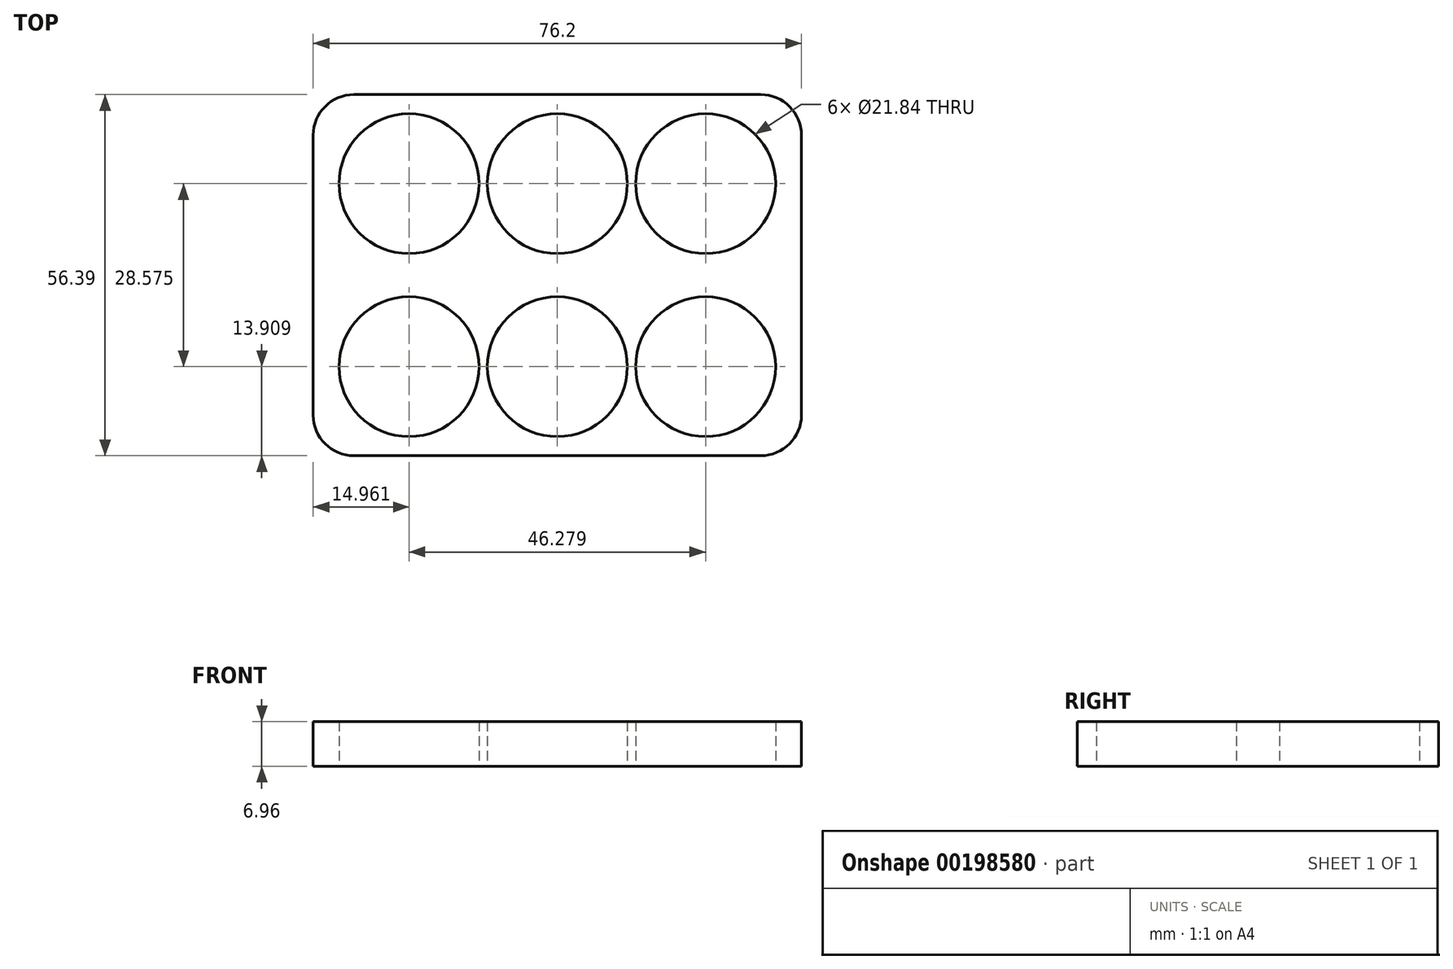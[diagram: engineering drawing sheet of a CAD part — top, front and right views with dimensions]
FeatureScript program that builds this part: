
annotation { "Feature Type Name" : "Feature", "Feature Type Description" : "" }
export const myFeature = defineFeature(function(context is Context, id is Id, definition is map)
    precondition{}
    {
        {
            var Q0;
            Q0=qCreatedBy(makeId("Top.planeOp"),FACE);
            var sketch = newSketch(context, id + "F0", { "sketchPlane" : qUnion([Q0])});
            skLineSegment(sketch, "E0", {"start": v(-31.75, 0) * mm, "end": v(31.75, 0) * mm});
            skArc(sketch, "E1", {"start": v(-31.75, 0) * mm, "mid": v(-36.24, -1.86) * mm, "end": v(-38.1, -6.35) * mm});
            skLineSegment(sketch, "E2", {"start": v(-38.1, -6.35) * mm, "end": v(-38.1, -50.04) * mm});
            skArc(sketch, "E3", {"start": v(-38.1, -50.04) * mm, "mid": v(-36.24, -54.53) * mm, "end": v(-31.75, -56.39) * mm});
            skLineSegment(sketch, "E4", {"start": v(-31.75, -56.39) * mm, "end": v(31.75, -56.39) * mm});
            skArc(sketch, "E5", {"start": v(31.75, -56.39) * mm, "mid": v(36.24, -54.53) * mm, "end": v(38.1, -50.04) * mm});
            skLineSegment(sketch, "E6", {"start": v(38.1, -50.04) * mm, "end": v(38.1, -6.35) * mm});
            skArc(sketch, "E7", {"start": v(38.1, -6.35) * mm, "mid": v(36.24, -1.86) * mm, "end": v(31.75, 0) * mm});
            skLineSegment(sketch, "E8", {"start": v(38.1, -28.2) * mm, "end": v(-38.1, -28.2) * mm, "construction": true});
            skLineSegment(sketch, "E9", {"start": v(0, 0) * mm, "end": v(0, -56.39) * mm, "construction": true});
            skCircle(sketch, "E10", {"center": v(-23.14, -13.9) * mm, "radius": 10.92 * mm});
            skCircle(sketch, "E11", {"center": v(0, -13.9) * mm, "radius": 10.92 * mm});
            skCircle(sketch, "E12", {"center": v(23.14, -13.9) * mm, "radius": 10.92 * mm});
            skCircle(sketch, "E13", {"center": v(-23.14, -42.48) * mm, "radius": 10.92 * mm});
            skCircle(sketch, "E14", {"center": v(0, -42.48) * mm, "radius": 10.92 * mm});
            skCircle(sketch, "E15", {"center": v(23.14, -42.48) * mm, "radius": 10.92 * mm});
            skLineSegment(sketch, "E16", {"start": v(-23.14, -13.9) * mm, "end": v(-23.14, -42.48) * mm, "construction": true});
            skLineSegment(sketch, "E17", {"start": v(23.14, -13.9) * mm, "end": v(23.14, -42.48) * mm, "construction": true});
            skLineSegment(sketch, "E18", {"start": v(-23.14, -13.9) * mm, "end": v(23.14, -13.9) * mm, "construction": true});
            skLineSegment(sketch, "E19", {"start": v(-23.14, -42.48) * mm, "end": v(23.14, -42.48) * mm, "construction": true});
            skSolve(sketch);
        }
        {
            var Q0;
            Q0=makeQuery(id+"F0.imprint","IMPRINT",FACE,{"disambiguationData":[TD([[makeQuery(id+"F0.imprint","IMPRINT",EDGE,{"derivedFrom":sQuery(id+"F0.wireOp",EDGE,"E0")}),-1.0]])]});
            extrude(context, id + "F1", {"entities" : qUnion([Q0]), "depth" : 6.96 * mm});
        }
    });
